# Revit family: HD076-2016.05.17-BT-_Cielo_Baffle_50
name_source: partatom
category: Modelos genéricos
revit_build: Autodesk Revit 2017 (Build: 20160225_1515(x64)
units: mm (PartAtom-declared; Revit-internal decimal feet)

## family parameters
Compartido = No
Corte con vacíos al cargar = No
Cota de conector redondo = Diámetro de uso
Puede alojar armadura = No
Punto de cálculo de habitación = No
Se basa en plano de trabajo = No
Siempre vertical = Sí
Tipo de pieza = Normal

## types (1)
- Productos HD
    BT_Alto = 50 mm
    BT_Ancho = 25 mm
    BT_Codigo_Origen = HD076
    BT_Color = 100 colores a eleccion
    BT_Código_Línea = De Linea
    BT_Descripcion = Cielo Baffle 50 Paso 75
    BT_EETT = El cielo Baffle es un cielo lineal que consiste en paneles dispuestos paralelamente soportados por un portapanel
    BT_Elemento = Cielos
    BT_Especialidad = Arquitectura
    BT_Fabricante = Hunter Douglas
    BT_Itemizado_Estandar_CDT = D 04 04 80
    BT_Marca = Hunter Douglas
    BT_MasterFormat® = 09 54 23
    BT_Material = Aluminio / Aluzinc
    BT_Nombre_Corto = Cielo Baffle 50 Paso 75
    BT_Nombre_Tecnico = Cielo Baffle 50 Paso 75
    BT_Peso = 9.68 Kg/m2
    BT_Profundidad = Largo Máximo 6 mts
    BT_SKU = 003598
    BT_Uso = Interior
    BT_Web_del_Producto = http://www.hunterdouglas.cl
    Cantidad Paneles = 15
    ID_Objeto = BT_F_F_698
    ID_Source = BIMTOOL
    Material = Phase - Demo

## geometry (parser evidence)
native form markers: Blend x8, Sweep x49
no freeform markers — native parametric forms only
